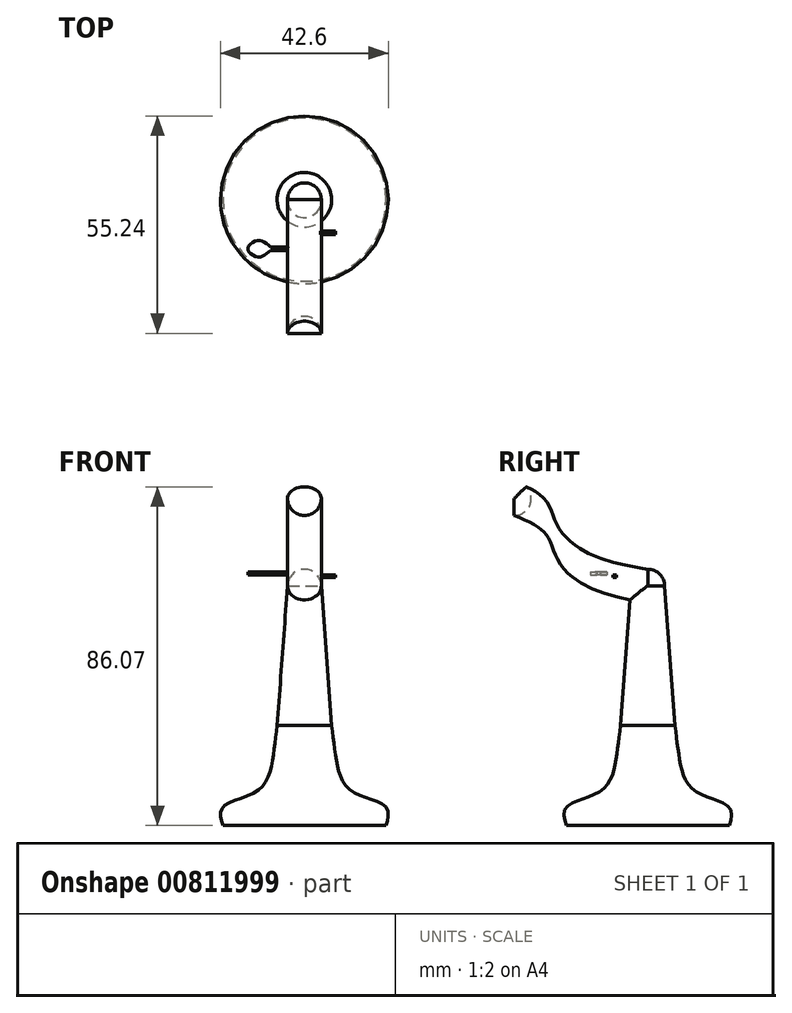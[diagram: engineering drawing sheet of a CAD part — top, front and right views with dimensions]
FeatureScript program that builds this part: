
annotation { "Feature Type Name" : "Feature", "Feature Type Description" : "" }
export const myFeature = defineFeature(function(context is Context, id is Id, definition is map)
    precondition{}
    {
        {
            var Q0;
            Q0=qCreatedBy(makeId("Front.planeOp"),FACE);
            var sketch = newSketch(context, id + "F0", { "sketchPlane" : qUnion([Q0])});
            skLineSegment(sketch, "E0", {"start": v(0, -39.33) * mm, "end": v(20.71, -39.33) * mm});
            skFitSpline(sketch, "E1", {"points": [v(20.71, -39.33) * mm, v(20.71, -34.7) * mm, v(11.84, -30.42) * mm, v(8.22, -23.27) * mm, v(6.93, -13.91) * mm], "startDerivative": vector(7.95, 26.78) * mm, "endDerivative": vector(-3.92, 34.59) * mm});
            skLineSegment(sketch, "E2", {"start": v(6.93, -13.91) * mm, "end": v(4.3, 21.5) * mm});
            skLineSegment(sketch, "E3", {"start": v(0, -39.33) * mm, "end": v(0, 21.5) * mm});
            skLineSegment(sketch, "E4", {"start": v(0, 21.5) * mm, "end": v(4.3, 21.5) * mm});
            skSolve(sketch);
        }
        {
            var Q0;
            Q0=makeQuery(id+"F0.imprint","IMPRINT",FACE,{"disambiguationData":[TD([[makeQuery(id+"F0.imprint","IMPRINT",EDGE,{"derivedFrom":sQuery(id+"F0.wireOp",EDGE,"E0")}),1.0]])]});
            var Q1;
            Q1=sQuery(id+"F0.wireOp",EDGE,"E3");
            revolve(context, id + "F1", {"surfaceOperationType" : NewSurfaceOperationType.NEW, "entities" : qUnion([Q0]), "axis" : qUnion([Q1]), "revolveType" : RevolveType.FULL});
        }
        {
            var Q0;
            Q0=makeQuery(id+"F1.opRevolve","SWEPT_FACE",FACE,{"disambiguationData":[OSD([sQuery(id+"F0.wireOp",EDGE,"E4")])]});
            var sketch = newSketch(context, id + "F2", { "sketchPlane" : qUnion([Q0])});
            skCircle(sketch, "E5", {"center": v(0, 0) * mm, "radius": 4.37 * mm});
            skLineSegment(sketch, "E6", {"start": v(-4.3, 0) * mm, "end": v(4.3, 0) * mm});
            skSolve(sketch);
        }
        {
            var Q0;
            {var subQ0=sQuery(id+"F2.wireOp",EDGE,"E6");Q0=makeQuery(id+"F2.imprint","IMPRINT",FACE,{"disambiguationData":[TD([[makeQuery(id+"F2.imprint","IMPRINT",EDGE,{"derivedFrom":subQ0}),1.0]])]});}
            var Q1;
            Q1=sQuery(id+"F2.wireOp",EDGE,"E6");
            revolve(context, id + "F3", {"operationType" : NewBodyOperationType.ADD, "surfaceOperationType" : NewSurfaceOperationType.NEW, "entities" : qUnion([Q0]), "axis" : qUnion([Q1]), "revolveType" : RevolveType.ONE_DIRECTION, "angle" : 90 * degree});
        }
        {
            var Q0;
            Q0=makeQuery(id+"F3.opRevolve","CAP_FACE",FACE,{"disambiguationData":[OSD([sQuery(id+"F0.wireOp",EDGE,"E2"),sQuery(id+"F0.wireOp",EDGE,"E4"),sQuery(id+"F2.wireOp",EDGE,"E6")])],"isStart":false});
            var sketch = newSketch(context, id + "F4", { "sketchPlane" : qUnion([Q0])});
            skCircle(sketch, "E7", {"center": v(0, 21.5) * mm, "radius": 4.3 * mm});
            skSolve(sketch);
        }
        {
            var Q0;
            Q0=qCreatedBy(makeId("Right.planeOp"),FACE);
            var sketch = newSketch(context, id + "F5", { "sketchPlane" : qUnion([Q0])});
            skFitSpline(sketch, "E8", {"points": [v(0, 21.5) * mm, v(-13.86, 25.04) * mm, v(-22.53, 31.84) * mm, v(-25.96, 39.07) * mm, v(-33.94, 43.76) * mm], "startDerivative": vector(-49.6, 8.77) * mm, "endDerivative": vector(-40.07, 16.14) * mm});
            skSolve(sketch);
        }
        {
            var Q0;
            Q0 = qSketchRegion(id + "F4", true);
            var Q1;
            Q1 = qConstructionFilter(qBodyType(qCreatedBy(id + "F5" ,EDGE), BodyType.WIRE), ConstructionObject.NO);
            sweep(context, id + "F6", {"operationType" : NewBodyOperationType.ADD, "profiles" : qUnion([Q0]), "path" : qUnion([Q1]), "keepProfileOrientation" : true});
        }
        {
            var Q0;
            Q0=makeQuery(id+"F6.opSweep","CAP_FACE",FACE,{"disambiguationData":[OSD([sQuery(id+"F4.wireOp",EDGE,"E7"),sQuery(id+"F5.wireOp",VERTEX,"E8.end")])],"isStart":false});
            var sketch = newSketch(context, id + "F7", { "sketchPlane" : qUnion([Q0])});
            skLineSegment(sketch, "E9", {"start": v(0, 39.45) * mm, "end": v(0, 48.04) * mm});
            skSolve(sketch);
        }
        {
            var Q0;
            {var subQ0=sQuery(id+"F7.wireOp",EDGE,"E9");Q0=makeQuery(id+"F7.imprint","IMPRINT",FACE,{"disambiguationData":[TD([[makeQuery(id+"F7.imprint","IMPRINT",EDGE,{"derivedFrom":subQ0}),1.0]])]});}
            var Q1;
            Q1=sQuery(id+"F7.wireOp",EDGE,"E9");
            revolve(context, id + "F8", {"operationType" : NewBodyOperationType.ADD, "surfaceOperationType" : NewSurfaceOperationType.NEW, "entities" : qUnion([Q0]), "axis" : qUnion([Q1]), "revolveType" : RevolveType.FULL});
        }
        {
            var Q0;
            Q0=qCreatedBy(makeId("Right.planeOp"),FACE);
            var sketch = newSketch(context, id + "F9", { "sketchPlane" : qUnion([Q0])});
            skLineSegment(sketch, "E10.bottom", {"start": v(-7.93, 24.4) * mm, "end": v(-8.83, 24.4) * mm});
            skLineSegment(sketch, "E10.top", {"start": v(-7.93, 23.73) * mm, "end": v(-8.83, 23.73) * mm});
            skLineSegment(sketch, "E10.left", {"start": v(-7.93, 24.4) * mm, "end": v(-7.93, 23.73) * mm});
            skLineSegment(sketch, "E10.right", {"start": v(-8.83, 24.4) * mm, "end": v(-8.83, 23.73) * mm});
            skSolve(sketch);
        }
        {
            var Q0;
            Q0 = qSketchRegion(id + "F9", true);
            extrude(context, id + "F10", {"entities" : qUnion([Q0]), "operationType" : NewBodyOperationType.ADD, "depth" : 7.87 * mm, "offsetDistance" : 25.4 * mm});
        }
        {
            var Q0;
            Q0=qCreatedBy(makeId("Right.planeOp"),FACE);
            var sketch = newSketch(context, id + "F11", { "sketchPlane" : qUnion([Q0])});
            skLineSegment(sketch, "E11.bottom", {"start": v(-12.87, 25.12) * mm, "end": v(-12, 25.12) * mm});
            skLineSegment(sketch, "E11.top", {"start": v(-12.87, 24.32) * mm, "end": v(-12, 24.32) * mm});
            skLineSegment(sketch, "E11.left", {"start": v(-12.87, 25.12) * mm, "end": v(-12.87, 24.32) * mm});
            skLineSegment(sketch, "E11.right", {"start": v(-12, 25.12) * mm, "end": v(-12, 24.32) * mm});
            skSolve(sketch);
        }
        {
            var Q0;
            Q0 = qSketchRegion(id + "F11", true);
            extrude(context, id + "F12", {"entities" : qUnion([Q0]), "operationType" : NewBodyOperationType.ADD, "oppositeDirection" : true, "depth" : 8.64 * mm, "offsetDistance" : 25.4 * mm});
        }
        {
            var Q0;
            Q0=makeQuery(id+"F12.opExtrude","SWEPT_FACE",FACE,{"disambiguationData":[OSD([sQuery(id+"F11.wireOp",EDGE,"E11.top")])]});
            var sketch = newSketch(context, id + "F13", { "sketchPlane" : qUnion([Q0])});
            skFitSpline(sketch, "E12", {"points": [v(-8.64, 12) * mm, v(-11.88, 10.37) * mm, v(-14.38, 12.5) * mm, v(-11.63, 14.53) * mm, v(-8.64, 12.87) * mm], "startDerivative": vector(-11.77, -10.24) * mm, "endDerivative": vector(10.76, -10.31) * mm});
            skSolve(sketch);
        }
        {
            var Q0;
            Q0 = qSketchRegion(id + "F13", true);
            var Q1;
            Q1=makeQuery(id+"F13.imprint","IMPRINT",FACE,{"disambiguationData":[TD([[makeQuery(id+"F13.imprint","IMPRINT",EDGE,{"derivedFrom":sQuery(id+"F13.wireOp",EDGE,"E12")}),-1.0]])]});
            extrude(context, id + "F14", {"entities" : qUnion([Q0, Q1]), "operationType" : NewBodyOperationType.ADD, "oppositeDirection" : true, "depth" : 0.79 * mm, "offsetDistance" : 25.4 * mm});
        }
    });
